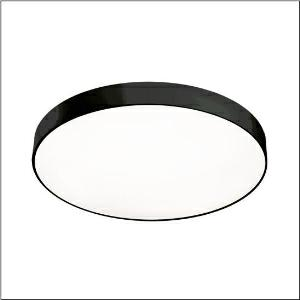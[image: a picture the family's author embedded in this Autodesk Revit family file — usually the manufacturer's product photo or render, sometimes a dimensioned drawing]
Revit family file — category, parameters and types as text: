
# Revit family: round_21_l_51mr38fd0421b
name_source: partatom
category: Lighting Fixtures
units: mm (PartAtom-declared; Revit-internal decimal feet)

## family parameters
Cut with Voids When Loaded = No
Host = Face
Light Source = No
Part Type = Normal
Room Calculation Point = No
Round Connector Dimension = Use Diameter
Shared = No

## types (1)
- Round 21 L (1 x LED, 14150 lm, 97 W, 4000K)
    Apparent Load = 97 VA
    CIE Flux Codes = 49 80 96 100 100
    Color Rendering = 80
    Color Temperature = 4000K
    Default Elevation = 1800 mm
    Description = Round 21 L, wall and ceiling luminaire, primary optical cover: cover, of PMMA, opal, light emission: direct distribution, primary light characteristic: symmetric, installation type: suspended mounting, surface-mounted, LED, rated luminous flux: 13.080lm, luminous efficacy: 146lm/W, light colour: 840, colour temperature: 4000K, with terminal, 5-pole, mains connection: 230V, AC, 50/60Hz, rated input power: 97W, housing, of aluminium, coated, black, diameter: 850mm, height: 62mm, protection rating (complete): IP40, insulation class (complete): insulation class I (protective earthing), certification: CE, impact resistance: IK04, permissible operating ambient temperature: -10..+35°C, packaging unit: 1 piece
    Height = 87 mm
    Lamp = 1 x LED
    Lamp Light Flux = 14150 lm
    Lamp Power = 97 W
    Lamp count = 1
    Length = 850 mm
    Luminous efficacy = 146 lm/W
    Manufacturer = Siteco
    ModVariant = No
    Model = 51MR38FD0421B
    Mounting Place = Ceiling
    Mounting Type = Surface mounted
    Number of Poles = 1
    OnlyDefault = Yes
    Power Factor = 1
    Product Name = Round 21 L
    Product group = wall and ceiling luminaire
    ProductGroupID = 303
    Protection Class = Protection class I
    Protection Degree = IP 40
    RLX_Detail_Level = 1
    RLX_Emergency_Light_Flux = 0 lm
    RLX_Emergency_Type = 0
    RLX_Emergency_Type_DB = No
    RlxData = <blob elided: 23893 chars, md5=357eca13>
    Socket = socket
    Standby Power = 0 W
    System Light Flux = 14150 lm
    System Power = 97 W
    Type Comments = Product without accessories
    Type Image = l_1258328.jpg
    URL = http://relux.com
    VarID = ---
    Voltage = 0 V
    Weight = 0.00 kg
    Width = 0 mm  [stored 0 ft]

note: [stored X ft] marks values corroborated as IEEE doubles in the binary element streams (Revit-internal decimal feet)

## geometry (parser evidence)
native form markers: Blend x4, Sweep x13
no freeform markers — native parametric forms only
